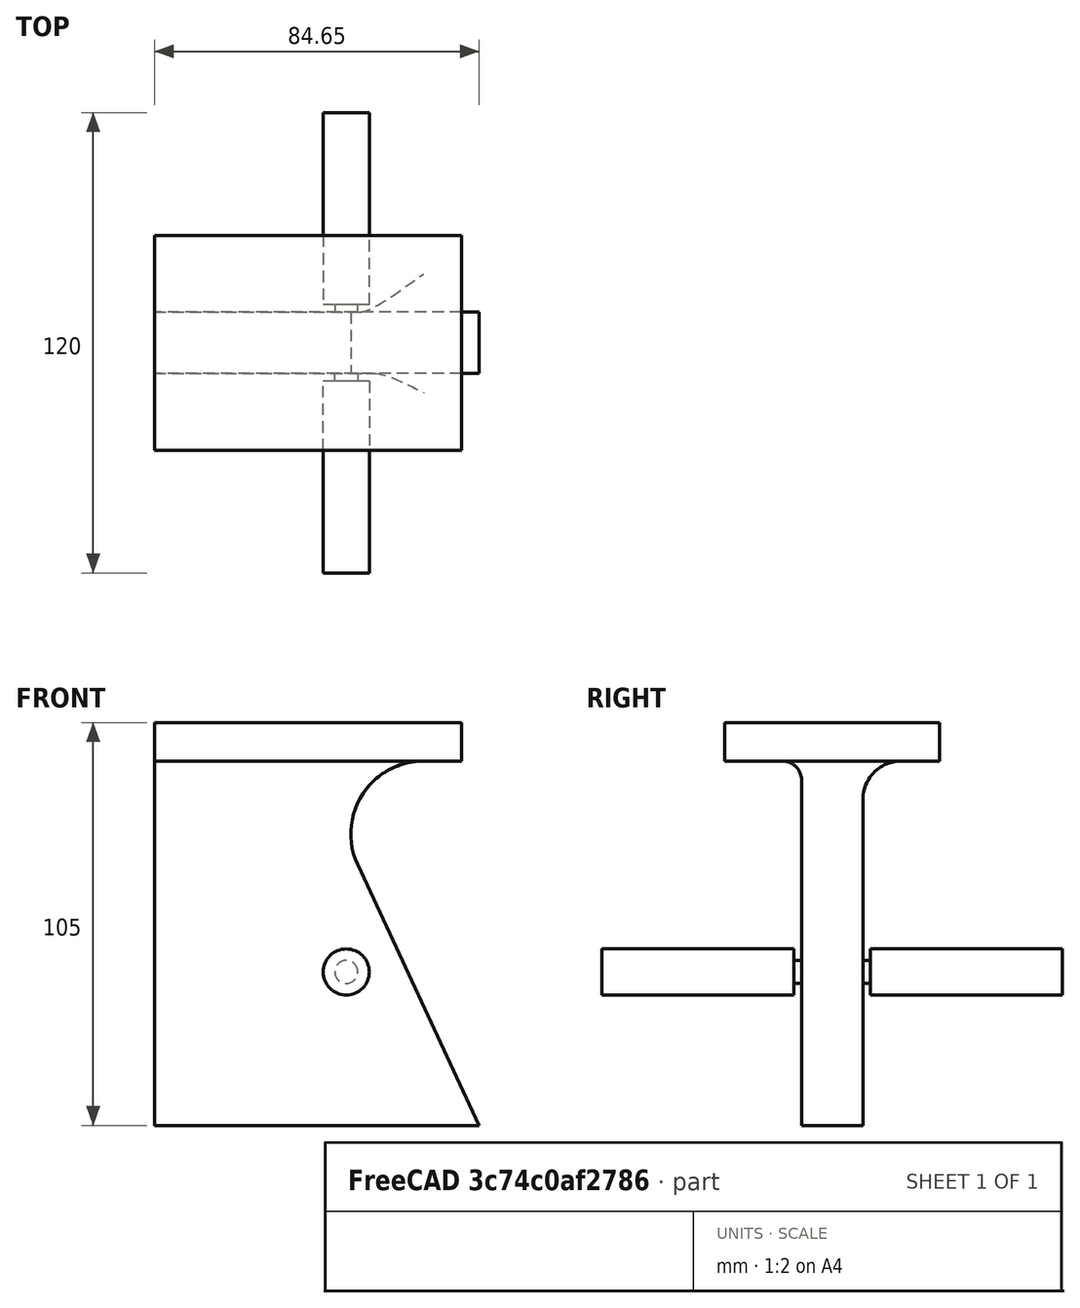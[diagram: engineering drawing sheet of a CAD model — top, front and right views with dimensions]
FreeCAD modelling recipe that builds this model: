
FCSTD DOCUMENT  (FreeCAD 1.0R38806 (Git))
Label: cx7 grip 20241022
License: All rights reserved
LicenseURL: http://en.wikipedia.org/wiki/All_rights_reserved
objects: Sketcher::SketchObject×4, PartDesign::Pad×4, PartDesign::Fillet×3, PartDesign::Mirrored×2, PartDesign::Body×1
note: 34 computed .brp shape members not serialized (recipe doc carries the construction recipe); baked Part::Feature solids carry a one-line shape summary decoded from their .brp

FEATURE [Sketcher::SketchObject] Sketch002
  ArcFitTolerance = 1e-06
  AttachmentSupport = -> [XZ_Plane001]
  FullyConstrained = true
  MakeInternals = false
  MapMode = 5
  Placement = pos=(0,0,0) rot=(1,0,0;1.5708rad)
  sketch-geometry (7):
    g0: LineSegment StartX=34.6523 StartY=-40 StartZ=0 EndX=-9.64692 EndY=55 EndZ=0
    g1: GeomPoint X=16 Y=0 Z=0
    g2: LineSegment StartX=34.6523 StartY=-40 StartZ=0 EndX=-50 EndY=-40 EndZ=0
    g3: LineSegment StartX=-50 StartY=-40 StartZ=0 EndX=-50 EndY=65 EndZ=0
    g4: LineSegment StartX=-50 StartY=65 StartZ=0 EndX=30 EndY=65 EndZ=0
    g5: LineSegment StartX=30 StartY=65 StartZ=0 EndX=30 EndY=55 EndZ=0
    g6: LineSegment StartX=30 StartY=55 StartZ=0 EndX=-9.64692 EndY=55 EndZ=0
  constraints (20):
    c: PointOnObject(g1,g-1)
    c: PointOnObject(g1,g0)
    c: DistanceX(g-1,g1) = 16
    c: DistanceY(g0,g-1) = 40
    c: Coincident(g2,g0)
    c: Horizontal(g2)
    c: Vertical(g3)
    c: Coincident(g4,g3)
    c: Horizontal(g4)
    c: Coincident(g5,g4)
    c: Vertical(g5)
    c: Coincident(g6,g5)
    c: Horizontal(g6)
    c: Coincident(g0,g6)
    c: Angle(g0,g2) = 1.13446
    c: DistanceY(g-1,g5) = 55
    c: Distance(g5) = 10
    c: Coincident(g2,g3)
    c: DistanceX(g-1,g5) = 30
    c: DistanceX(g3,g-1) = 50
FEATURE [PartDesign::Pad] Pad
  Direction = (0,-1,2e-16)
  Length = 16
  Length2 = 10
  Midplane = true
  Placement = pos=(0,0,0) rot=(1,0,0;1.5708rad)
  Profile = -> Sketch002
  ReferenceAxis = -> Sketch002 [N_Axis]
  Suppressed = false
  Type = 0
FEATURE [PartDesign::Fillet] Fillet
  Base = -> Pad [Edge2]
  BaseFeature = -> Pad
  Placement = pos=(0,0,0) rot=(1,0,0;1.5708rad)
  Radius = 19
  SupportTransform = false
  Suppressed = false
  UseAllEdges = false
FEATURE [Sketcher::SketchObject] Sketch
  ArcFitTolerance = 1e-06
  AttachmentSupport = -> [Fillet]
  ExternalGeometry = -> [Fillet]
  FullyConstrained = true
  MakeInternals = false
  MapMode = 5
  Placement = pos=(0,-8,0) rot=(1,0,0;1.5708rad)
  sketch-geometry (4):
    g0: LineSegment StartX=-50 StartY=65 StartZ=0 EndX=-50 EndY=55 EndZ=0
    g1: LineSegment StartX=-50 StartY=55 StartZ=0 EndX=30 EndY=55 EndZ=0
    g2: LineSegment StartX=30 StartY=55 StartZ=0 EndX=30 EndY=65 EndZ=0
    g3: LineSegment StartX=30 StartY=65 StartZ=0 EndX=-50 EndY=65 EndZ=0
  constraints (10):
    c: Coincident(g0,g1)
    c: Coincident(g1,g2)
    c: Coincident(g2,g3)
    c: Coincident(g3,g0)
    c: Vertical(g0)
    c: Vertical(g2)
    c: Horizontal(g1)
    c: Horizontal(g3)
    c: Coincident(g0,g-4)
    c: Coincident(g1,g-3)
FEATURE [PartDesign::Pad] Pad001
  BaseFeature = -> Fillet
  Direction = (0,-1,2e-16)
  Length = 20
  Length2 = 10
  Placement = pos=(0,0,0) rot=(1,0,0;1.5708rad)
  Profile = -> Sketch
  ReferenceAxis = -> Sketch [N_Axis]
  Suppressed = false
  Type = 0
FEATURE [PartDesign::Mirrored] Mirrored
  BaseFeature = -> Pad001
  MirrorPlane = -> XZ_Plane001
  Originals = -> [Pad001]
  Placement = pos=(0,0,0) rot=(1,0,0;1.5708rad)
  Suppressed = false
  TransformMode = 0
FEATURE [PartDesign::Fillet] Fillet001
  Base = -> Mirrored [Edge13]
  BaseFeature = -> Mirrored
  Placement = pos=(0,0,0) rot=(1,0,0;1.5708rad)
  Radius = 5
  SupportTransform = false
  Suppressed = false
  UseAllEdges = false
FEATURE [PartDesign::Fillet] Fillet002
  Base = -> Fillet001 [Edge19]
  BaseFeature = -> Fillet001
  Placement = pos=(0,0,0) rot=(1,0,0;1.5708rad)
  Radius = 10
  SupportTransform = false
  Suppressed = false
  UseAllEdges = false
FEATURE [Sketcher::SketchObject] Sketch003
  ArcFitTolerance = 1e-06
  AttachmentSupport = -> [Fillet002]
  FullyConstrained = true
  MakeInternals = false
  MapMode = 5
  Placement = pos=(0,-8,0) rot=(1,0,0;1.5708rad)
  sketch-geometry (1):
    g0: Circle CenterX=0 CenterY=0 CenterZ=0 NormalX=0 NormalY=0 NormalZ=1 AngleXU=0 Radius=3
  constraints (2):
    c: Diameter(g0) = 6
    c: Coincident(g0,g-1)
FEATURE [PartDesign::Pad] Pad002
  BaseFeature = -> Fillet002
  Direction = (0,-1,2e-16)
  Length = 2
  Length2 = 10
  Placement = pos=(0,0,0) rot=(1,0,0;1.5708rad)
  Profile = -> Sketch003
  ReferenceAxis = -> Sketch003 [N_Axis]
  Suppressed = false
  Type = 0
FEATURE [Sketcher::SketchObject] Sketch004
  ArcFitTolerance = 1e-06
  AttachmentSupport = -> [Pad002]
  FullyConstrained = true
  MakeInternals = false
  MapMode = 5
  Placement = pos=(0,-10,3.4e-15) rot=(1,0,0;1.5708rad)
  sketch-geometry (1):
    g0: Circle CenterX=0 CenterY=0 CenterZ=0 NormalX=0 NormalY=0 NormalZ=1 AngleXU=0 Radius=6
  constraints (2):
    c: Diameter(g0) = 12
    c: Coincident(g0,g-1)
FEATURE [PartDesign::Pad] Pad003
  BaseFeature = -> Pad002
  Direction = (0,-1,2e-16)
  Length = 50
  Length2 = 10
  Placement = pos=(0,0,0) rot=(1,0,0;1.5708rad)
  Profile = -> Sketch004
  ReferenceAxis = -> Sketch004 [N_Axis]
  Suppressed = false
  Type = 0
FEATURE [PartDesign::Mirrored] Mirrored001
  BaseFeature = -> Pad003
  MirrorPlane = -> XZ_Plane001
  Originals = -> [Pad002,Pad003]
  Placement = pos=(0,0,0) rot=(1,0,0;1.5708rad)
  Suppressed = false
  TransformMode = 0
FEATURE [PartDesign::Body] Body
  AllowCompound = false
  Group = -> [Sketch002,Pad,Fillet,Sketch,Pad001,Mirrored,Fillet001,Fillet002,Sketch003,Pad002,Sketch004,Pad003,Mirrored001]
  Origin = -> Origin001
  Tip = -> Mirrored001
